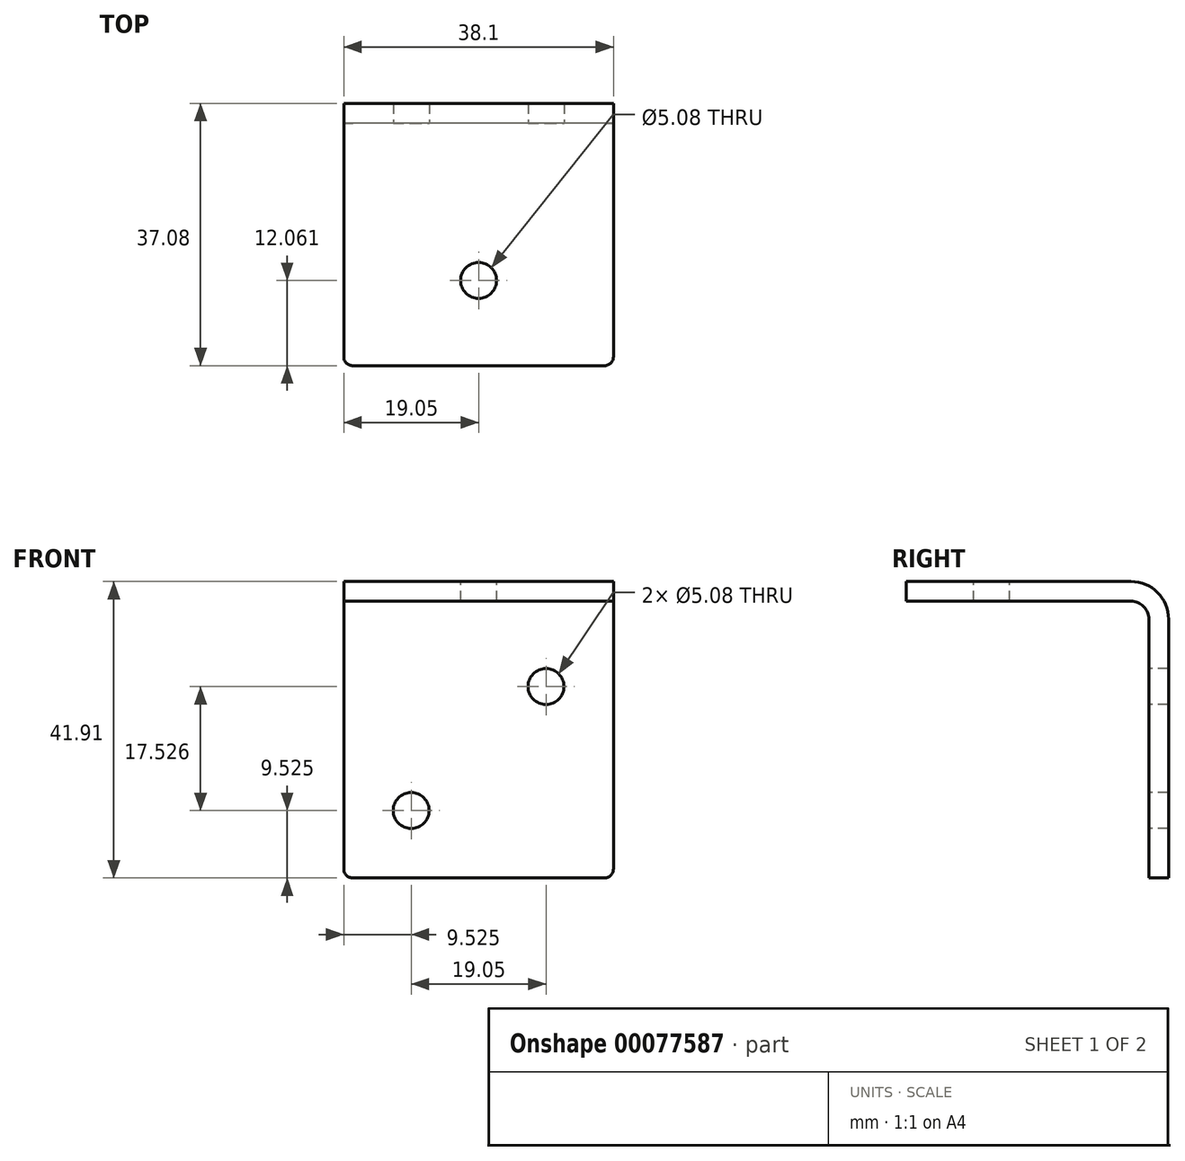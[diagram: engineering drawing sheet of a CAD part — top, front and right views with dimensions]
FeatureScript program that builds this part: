
annotation { "Feature Type Name" : "Feature", "Feature Type Description" : "" }
export const myFeature = defineFeature(function(context is Context, id is Id, definition is map)
    precondition{}
    {
        {
            var Q0;
            Q0=qCreatedBy(makeId("Right.planeOp"),FACE);
            var sketch = newSketch(context, id + "F0", { "sketchPlane" : qUnion([Q0])});
            skLineSegment(sketch, "E0.bottom", {"start": v(0, 0) * mm, "end": v(-2.8, 0) * mm});
            skLineSegment(sketch, "E0.left", {"start": v(0, 0) * mm, "end": v(0, 36.58) * mm});
            skLineSegment(sketch, "E0.right", {"start": v(-2.8, 0) * mm, "end": v(-2.8, 36.58) * mm});
            skLineSegment(sketch, "E1.top", {"start": v(-5.33, 39.12) * mm, "end": v(-37.08, 39.12) * mm});
            skLineSegment(sketch, "E1.right", {"start": v(-37.08, 41.91) * mm, "end": v(-37.08, 39.12) * mm});
            skPoint(sketch, "E2.visualSharp", {"position": v(-2.8, 39.12) * mm});
            skArc(sketch, "E2.filletArc", {"start": v(-2.8, 36.58) * mm, "mid": v(-3.54, 38.37) * mm, "end": v(-5.33, 39.12) * mm});
            skLineSegment(sketch, "E3", {"start": v(-37.08, 41.91) * mm, "end": v(-5.33, 41.91) * mm});
            skPoint(sketch, "E4.visualSharp", {"position": v(0, 41.91) * mm});
            skArc(sketch, "E4.filletArc", {"start": v(0, 36.58) * mm, "mid": v(-1.56, 40.35) * mm, "end": v(-5.33, 41.91) * mm});
            skSolve(sketch);
        }
        {
            var Q0;
            Q0 = qSketchRegion(id + "F0", true);
            extrude(context, id + "F1", {"entities" : qUnion([Q0]), "depth" : 38.1 * mm});
        }
        {
            var Q0;
            Q0=makeQuery(id+"F1.opExtrude","CAP_EDGE",EDGE,{"disambiguationData":[OSD([sQuery(id+"F0.wireOp",EDGE,"E1.right")])],"isStart":true});
            var Q1;
            Q1=makeQuery(id+"F1.opExtrude","CAP_EDGE",EDGE,{"disambiguationData":[OSD([sQuery(id+"F0.wireOp",EDGE,"E1.right")])],"isStart":false});
            var Q2;
            Q2=makeQuery(id+"F1.opExtrude","CAP_EDGE",EDGE,{"disambiguationData":[OSD([sQuery(id+"F0.wireOp",EDGE,"E0.bottom")])],"isStart":false});
            var Q3;
            Q3=makeQuery(id+"F1.opExtrude","CAP_EDGE",EDGE,{"disambiguationData":[OSD([sQuery(id+"F0.wireOp",EDGE,"E0.bottom")])],"isStart":true});
            fillet(context, id + "F2", {"entities" : qUnion([Q0, Q1, Q2, Q3]), "radius" : 1.27 * mm, "tangentPropagation" : true, "allowEdgeOverflow" : false});
        }
        {
            var Q0;
            Q0=makeQuery(id+"F1.opExtrude","SWEPT_FACE",FACE,{"disambiguationData":[OSD([sQuery(id+"F0.wireOp",EDGE,"E3")])]});
            var sketch = newSketch(context, id + "F3", { "sketchPlane" : qUnion([Q0])});
            skLineSegment(sketch, "E5", {"start": v(19.05, -37.08) * mm, "end": v(19.05, -5.33) * mm, "construction": true});
            skCircle(sketch, "E6", {"center": v(19.05, -25.02) * mm, "radius": 2.54 * mm});
            skSolve(sketch);
        }
        {
            var Q0;
            Q0 = qSketchRegion(id + "F3", true);
            extrude(context, id + "F4", {"entities" : qUnion([Q0]), "operationType" : NewBodyOperationType.REMOVE, "endBound" : BoundingType.UP_TO_NEXT, "oppositeDirection" : true, "depth" : 25.4 * mm});
        }
        {
            var Q0;
            Q0=makeQuery(id+"F1.opExtrude","SWEPT_FACE",FACE,{"disambiguationData":[OSD([sQuery(id+"F0.wireOp",EDGE,"E0.right")])]});
            var sketch = newSketch(context, id + "F5", { "sketchPlane" : qUnion([Q0])});
            skCircle(sketch, "E7", {"center": v(28.58, 27.05) * mm, "radius": 2.54 * mm});
            skCircle(sketch, "E8", {"center": v(9.53, 9.52) * mm, "radius": 2.54 * mm});
            skLineSegment(sketch, "E9", {"start": v(38.1, 27.05) * mm, "end": v(28.58, 27.05) * mm, "construction": true});
            skLineSegment(sketch, "E10", {"start": v(0, 9.53) * mm, "end": v(9.53, 9.53) * mm, "construction": true});
            skLineSegment(sketch, "E11", {"start": v(9.53, 9.52) * mm, "end": v(9.53, 0) * mm, "construction": true});
            skLineSegment(sketch, "E12", {"start": v(28.58, 27.05) * mm, "end": v(28.58, 36.58) * mm, "construction": true});
            skSolve(sketch);
        }
        {
            var Q0;
            Q0 = qSketchRegion(id + "F5", true);
            extrude(context, id + "F6", {"entities" : qUnion([Q0]), "operationType" : NewBodyOperationType.REMOVE, "endBound" : BoundingType.UP_TO_NEXT, "oppositeDirection" : true, "depth" : 25.4 * mm});
        }
    });
